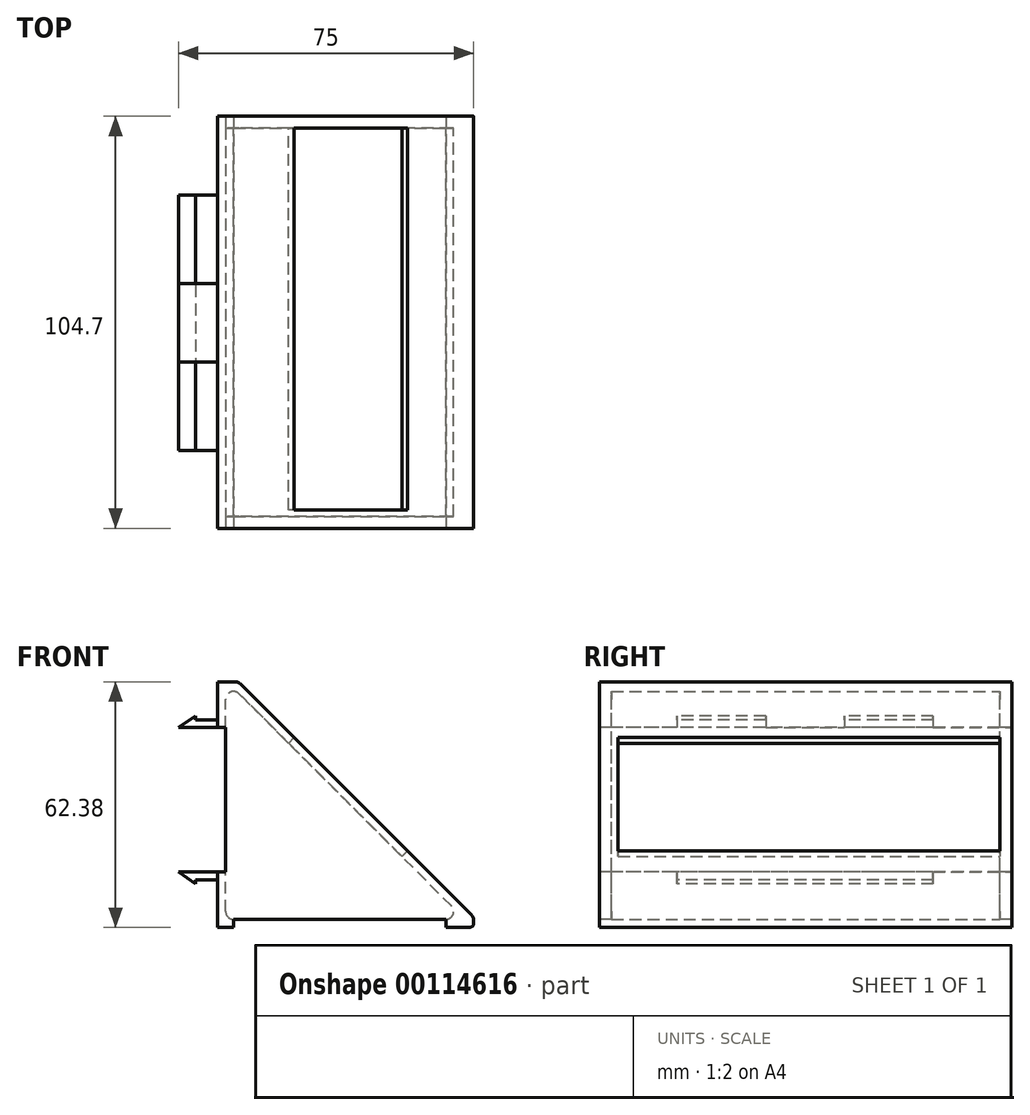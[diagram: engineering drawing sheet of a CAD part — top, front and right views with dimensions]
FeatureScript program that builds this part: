
annotation { "Feature Type Name" : "Feature", "Feature Type Description" : "" }
export const myFeature = defineFeature(function(context is Context, id is Id, definition is map)
    precondition{}
    {
        {
            var Q0;
            Q0=qCreatedBy(makeId("Front.planeOp"),FACE);
            var sketch = newSketch(context, id + "F0", { "sketchPlane" : qUnion([Q0])});
            skLineSegment(sketch, "E0", {"start": v(0, 0) * mm, "end": v(0, 62.38) * mm});
            skLineSegment(sketch, "E1", {"start": v(0, 62.38) * mm, "end": v(4.38, 62.38) * mm});
            skLineSegment(sketch, "E2", {"start": v(65, 1) * mm, "end": v(65, 1.76) * mm});
            skLineSegment(sketch, "E3", {"start": v(64.41, 3.17) * mm, "end": v(5.8, 61.8) * mm});
            skPoint(sketch, "E4.visualSharp", {"position": v(0, 62.38) * mm});
            skPoint(sketch, "E5.visualSharp", {"position": v(5, 62.38) * mm});
            skArc(sketch, "E5.filletArc", {"start": v(5.8, 61.8) * mm, "mid": v(5.14, 62.23) * mm, "end": v(4.38, 62.38) * mm});
            skPoint(sketch, "E6.visualSharp", {"position": v(65, 2.59) * mm});
            skPoint(sketch, "E7.visualSharp", {"position": v(65, 0) * mm});
            skLineSegment(sketch, "E8.0", {"start": v(59.34, 5.41) * mm, "end": v(5.41, 59.34) * mm});
            skLineSegment(sketch, "E9.0", {"start": v(4, 2) * mm, "end": v(57.93, 2) * mm});
            skPoint(sketch, "E10.visualSharp", {"position": v(62.76, 2) * mm});
            skArc(sketch, "E10.filletArc", {"start": v(57.93, 2) * mm, "mid": v(59.78, 3.23) * mm, "end": v(59.34, 5.41) * mm});
            skLineSegment(sketch, "E11.0", {"start": v(2, 4) * mm, "end": v(2, 57.93) * mm});
            skArc(sketch, "E12.filletArc", {"start": v(2, 4) * mm, "mid": v(2.59, 2.59) * mm, "end": v(4, 2) * mm});
            skArc(sketch, "E13.filletArc", {"start": v(5.41, 59.34) * mm, "mid": v(3.23, 59.78) * mm, "end": v(2, 57.93) * mm});
            skLineSegment(sketch, "E14", {"start": v(19.4, 48.18) * mm, "end": v(17.99, 46.77) * mm});
            skLineSegment(sketch, "E15", {"start": v(0, 32.38) * mm, "end": v(32.38, 32.38) * mm, "construction": true});
            skLineSegment(sketch, "E16", {"start": v(2, 50.73) * mm, "end": v(0, 50.73) * mm});
            skLineSegment(sketch, "E17", {"start": v(0, 0) * mm, "end": v(33.8, 33.8) * mm, "construction": true});
            skLineSegment(sketch, "E18", {"start": v(0, 0) * mm, "end": v(64, 0) * mm});
            skArc(sketch, "E19.filletArc", {"start": v(64, 0) * mm, "mid": v(64.7, 0.3) * mm, "end": v(65, 1) * mm});
            skArc(sketch, "E20.filletArc", {"start": v(65, 1.76) * mm, "mid": v(64.85, 2.52) * mm, "end": v(64.41, 3.17) * mm});
            skLineSegment(sketch, "E21", {"start": v(0, 50.73) * mm, "end": v(-10, 50.73) * mm});
            skLineSegment(sketch, "E22", {"start": v(-10, 50.73) * mm, "end": v(-5.6, 53.73) * mm});
            skLineSegment(sketch, "E23", {"start": v(-5.6, 53.73) * mm, "end": v(-5.6, 52.73) * mm});
            skLineSegment(sketch, "E24", {"start": v(-5.6, 52.73) * mm, "end": v(0, 52.73) * mm});
            skLineSegment(sketch, "E25.MirrorCS", {"start": v(0, 14.03) * mm, "end": v(-10, 14.03) * mm});
            skLineSegment(sketch, "E26.MirrorCS", {"start": v(-5.6, 12.03) * mm, "end": v(0, 12.03) * mm});
            skLineSegment(sketch, "E27.MirrorCS", {"start": v(-5.6, 11.03) * mm, "end": v(-5.6, 12.03) * mm});
            skLineSegment(sketch, "E28.MirrorCS", {"start": v(-10, 14.03) * mm, "end": v(-5.6, 11.03) * mm});
            skLineSegment(sketch, "E29.MirrorCS", {"start": v(48.18, 19.4) * mm, "end": v(46.77, 17.99) * mm});
            skLineSegment(sketch, "E30.MirrorCS", {"start": v(2, 14.03) * mm, "end": v(0, 14.03) * mm});
            skLineSegment(sketch, "E31", {"start": v(57.93, 2) * mm, "end": v(57.93, 0) * mm});
            skLineSegment(sketch, "E32", {"start": v(4, 2) * mm, "end": v(4, 0) * mm});
            skSolve(sketch);
        }
        {
            var Q0;
            {var subQ4=sQuery(id+"F0.wireOp",EDGE,"E1");Q0=makeQuery(id+"F0.imprint","IMPRINT",FACE,{"disambiguationData":[TD([[makeQuery(id+"F0.imprint","IMPRINT",EDGE,{"derivedFrom":subQ4}),-1.0]])]});}
            var Q1;
            Q1=makeQuery(id+"F0.imprint","IMPRINT",FACE,{"disambiguationData":[TD([[makeQuery(id+"F0.imprint","IMPRINT",EDGE,{"derivedFrom":sQuery(id+"F0.wireOp",EDGE,"E9.0")}),1.0]])]});
            var Q2;
            Q2=makeQuery(id+"F0.imprint","IMPRINT",FACE,{"disambiguationData":[TD([[makeQuery(id+"F0.imprint","IMPRINT",EDGE,{"derivedFrom":sQuery(id+"F0.wireOp",EDGE,"E2")}),1.0]])]});
            var Q3;
            {var subQ1=sQuery(id+"F0.wireOp",EDGE,"E25.MirrorCS");Q3=makeQuery(id+"F0.imprint","IMPRINT",FACE,{"disambiguationData":[TD([[makeQuery(id+"F0.imprint","IMPRINT",EDGE,{"derivedFrom":subQ1}),1.0]])]});}
            var Q4;
            {var subQ0=sQuery(id+"F0.wireOp",EDGE,"E21");Q4=makeQuery(id+"F0.imprint","IMPRINT",FACE,{"disambiguationData":[TD([[makeQuery(id+"F0.imprint","IMPRINT",EDGE,{"derivedFrom":subQ0}),-1.0]])]});}
            var Q5;
            {var subQ0=sQuery(id+"F0.wireOp",EDGE,"E14");Q5=makeQuery(id+"F0.imprint","IMPRINT",FACE,{"disambiguationData":[TD([[makeQuery(id+"F0.imprint","IMPRINT",EDGE,{"derivedFrom":subQ0}),1.0]])]});}
            var Q6;
            {var subQ0=sQuery(id+"F0.wireOp",EDGE,"E12.filletArc");Q6=makeQuery(id+"F0.imprint","IMPRINT",FACE,{"disambiguationData":[TD([[makeQuery(id+"F0.imprint","IMPRINT",EDGE,{"derivedFrom":subQ0}),-1.0]])]});}
            extrude(context, id + "F1", {"entities" : qUnion([Q0, Q1, Q2, Q3, Q4, Q5, Q6]), "oppositeDirection" : true, "depth" : 3 * mm, "hasSecondDirection" : true, "secondDirectionOppositeDirection" : false, "secondDirectionDepth" : (98.7 + 3) * mm});
        }
        {
            var Q0;
            Q0=makeQuery(id+"F0.imprint","IMPRINT",FACE,{"disambiguationData":[TD([[makeQuery(id+"F0.imprint","IMPRINT",EDGE,{"derivedFrom":sQuery(id+"F0.wireOp",EDGE,"E9.0")}),1.0]])]});
            extrude(context, id + "F2", {"entities" : qUnion([Q0]), "operationType" : NewBodyOperationType.REMOVE, "depth" : 98.7 * mm});
        }
        {
            var Q0;
            {var subQ0=sQuery(id+"F0.wireOp",EDGE,"E14");Q0=makeQuery(id+"F0.imprint","IMPRINT",FACE,{"disambiguationData":[TD([[makeQuery(id+"F0.imprint","IMPRINT",EDGE,{"derivedFrom":subQ0}),1.0]])]});}
            extrude(context, id + "F3", {"entities" : qUnion([Q0]), "operationType" : NewBodyOperationType.REMOVE, "depth" : 97 * mm});
        }
        {
            var Q0;
            Q0=makeQuery(id+"F1.opExtrude","SWEPT_FACE",FACE,{"disambiguationData":[OSD([sQuery(id+"F0.wireOp",EDGE,"E16"),sQuery(id+"F0.wireOp",EDGE,"E21")])]});
            var sketch = newSketch(context, id + "F4", { "sketchPlane" : qUnion([Q0])});
            skLineSegment(sketch, "E33.bottom", {"start": v(0, -3) * mm, "end": v(-10, -3) * mm});
            skLineSegment(sketch, "E33.top", {"start": v(0, 17) * mm, "end": v(-10, 17) * mm});
            skLineSegment(sketch, "E33.left", {"start": v(0, 17) * mm, "end": v(0, -3) * mm});
            skLineSegment(sketch, "E33.right", {"start": v(-10, 17) * mm, "end": v(-10, -3) * mm});
            skLineSegment(sketch, "E34", {"start": v(74.8, 49.5) * mm, "end": v(74.8, 0) * mm, "construction": true});
            skLineSegment(sketch, "E35", {"start": v(74.8, 49.5) * mm, "end": v(-57.22, 49.5) * mm, "construction": true});
            skLineSegment(sketch, "E36", {"start": v(0, 59.5) * mm, "end": v(-10, 59.5) * mm});
            skLineSegment(sketch, "E37", {"start": v(-10, 59.5) * mm, "end": v(-10, 49.5) * mm});
            skLineSegment(sketch, "E38", {"start": v(0, 59.5) * mm, "end": v(0, 49.5) * mm});
            skLineSegment(sketch, "E39.MirrorCS", {"start": v(0, 102) * mm, "end": v(-10, 102) * mm});
            skLineSegment(sketch, "E40.MirrorCS", {"start": v(0, 82) * mm, "end": v(0, 102) * mm});
            skLineSegment(sketch, "E41.MirrorCS", {"start": v(-10, 82) * mm, "end": v(-10, 102) * mm});
            skLineSegment(sketch, "E42.MirrorCS", {"start": v(0, 82) * mm, "end": v(-10, 82) * mm});
            skLineSegment(sketch, "E43.MirrorCS", {"start": v(0, 39.5) * mm, "end": v(-10, 39.5) * mm});
            skLineSegment(sketch, "E44.MirrorCS", {"start": v(0, 39.5) * mm, "end": v(0, 49.5) * mm});
            skLineSegment(sketch, "E45.MirrorCS", {"start": v(-10, 39.5) * mm, "end": v(-10, 49.5) * mm});
            skSolve(sketch);
        }
        {
            var Q0;
            Q0=makeQuery(id+"F4.imprint","IMPRINT",FACE,{"disambiguationData":[TD([[makeQuery(id+"F4.imprint","IMPRINT",EDGE,{"derivedFrom":sQuery(id+"F4.wireOp",EDGE,"E39.MirrorCS")}),1.0]])]});
            var Q1;
            Q1=makeQuery(id+"F4.imprint","IMPRINT",FACE,{"disambiguationData":[TD([[makeQuery(id+"F4.imprint","IMPRINT",EDGE,{"derivedFrom":sQuery(id+"F4.wireOp",EDGE,"E36")}),1.0]])]});
            var Q2;
            Q2=makeQuery(id+"F4.imprint","IMPRINT",FACE,{"disambiguationData":[TD([[makeQuery(id+"F4.imprint","IMPRINT",EDGE,{"derivedFrom":sQuery(id+"F4.wireOp",EDGE,"E33.bottom")}),-1.0]])]});
            var Q3;
            {var subQ0=sQuery(id+"F4.wireOp",EDGE,"E42.MirrorCS");Q3=makeQuery(id+"F4.imprint","IMPRINT",FACE,{"disambiguationData":[TD([[makeQuery(id+"F4.imprint","IMPRINT",EDGE,{"derivedFrom":subQ0}),-1.0]])]});}
            extrude(context, id + "F5", {"entities" : qUnion([Q0, Q1, Q2, Q3]), "operationType" : NewBodyOperationType.REMOVE, "oppositeDirection" : true, "depth" : 25 * mm});
        }
        {
            var Q0;
            Q0=makeQuery(id+"F1.opExtrude","SWEPT_FACE",FACE,{"disambiguationData":[OSD([sQuery(id+"F0.wireOp",EDGE,"E16"),sQuery(id+"F0.wireOp",EDGE,"E21")])]});
            var sketch = newSketch(context, id + "F6", { "sketchPlane" : qUnion([Q0])});
            skLineSegment(sketch, "E46.bottom", {"start": v(0, -3) * mm, "end": v(-10, -3) * mm});
            skLineSegment(sketch, "E46.top", {"start": v(0, 17) * mm, "end": v(-10, 17) * mm});
            skLineSegment(sketch, "E46.left", {"start": v(0, -3) * mm, "end": v(0, 17) * mm});
            skLineSegment(sketch, "E46.right", {"start": v(-10, -3) * mm, "end": v(-10, 17) * mm});
            skLineSegment(sketch, "E47.bottom", {"start": v(-10, 81.7) * mm, "end": v(0, 81.7) * mm});
            skLineSegment(sketch, "E47.top", {"start": v(-10, 101.7) * mm, "end": v(0, 101.7) * mm});
            skLineSegment(sketch, "E47.left", {"start": v(-10, 81.7) * mm, "end": v(-10, 101.7) * mm});
            skLineSegment(sketch, "E47.right", {"start": v(0, 81.7) * mm, "end": v(0, 101.7) * mm});
            skSolve(sketch);
        }
        {
            var Q0;
            Q0=makeQuery(id+"F6.imprint","IMPRINT",FACE,{"disambiguationData":[TD([[makeQuery(id+"F6.imprint","IMPRINT",EDGE,{"derivedFrom":sQuery(id+"F6.wireOp",EDGE,"E46.bottom")}),-1.0]])]});
            var Q1;
            {var subQ0=sQuery(id+"F6.wireOp",EDGE,"E47.top");Q1=makeQuery(id+"F6.imprint","IMPRINT",FACE,{"disambiguationData":[TD([[makeQuery(id+"F6.imprint","IMPRINT",EDGE,{"derivedFrom":subQ0}),-1.0]])]});}
            extrude(context, id + "F7", {"entities" : qUnion([Q0, Q1]), "operationType" : NewBodyOperationType.REMOVE, "depth" : 50 * mm});
        }
    });
